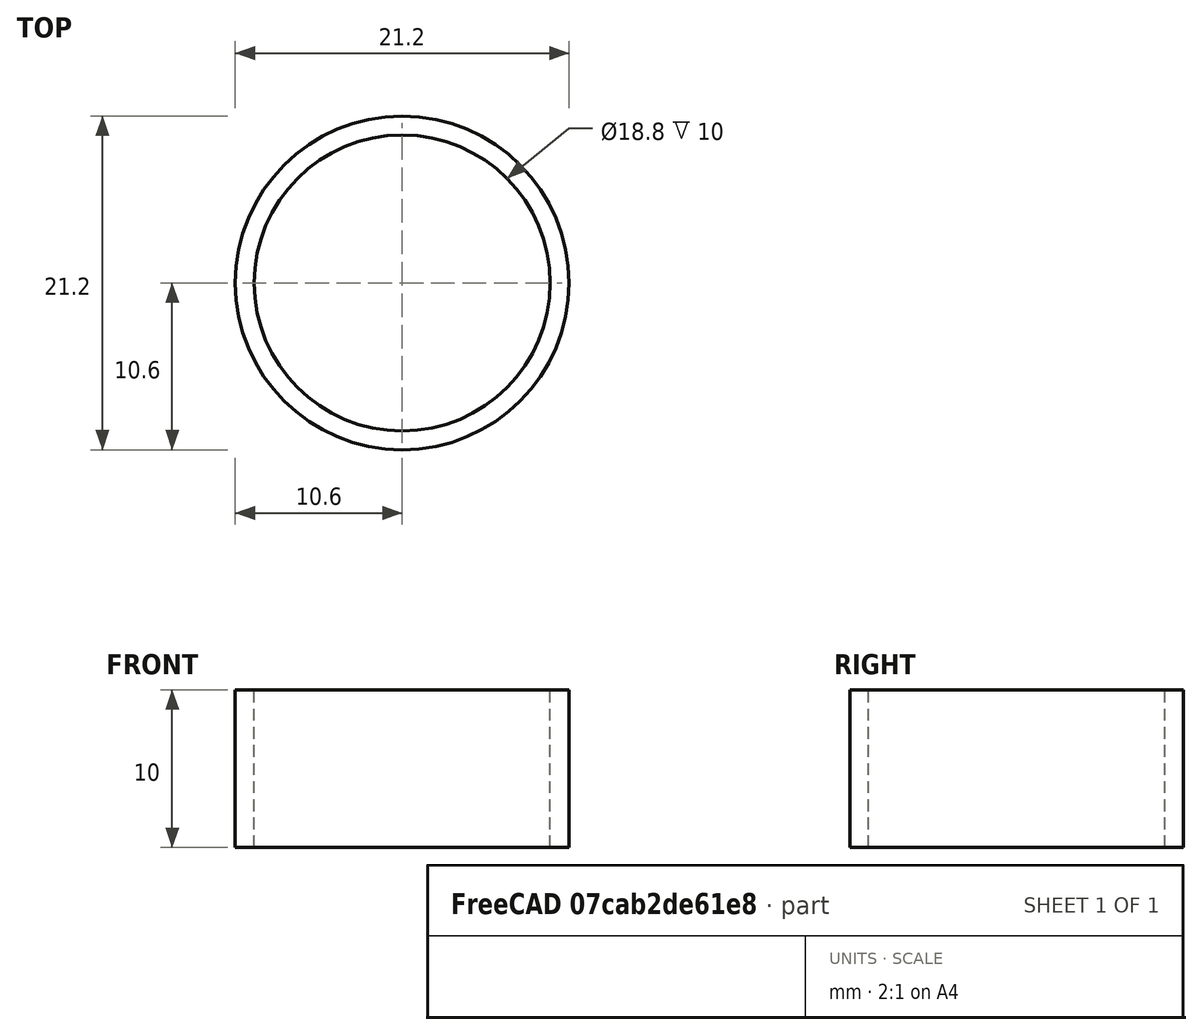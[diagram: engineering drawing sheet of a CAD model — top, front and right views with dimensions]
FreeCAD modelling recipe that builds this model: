
FCSTD DOCUMENT  (FreeCAD 0.20R29177 +426 (Git))
Label: Mag_Spacer_Outer
License: All rights reserved
LicenseURL: http://en.wikipedia.org/wiki/All_rights_reserved
objects: Sketcher::SketchObject×1, PartDesign::Revolution×1, PartDesign::Body×1
note: 4 computed .brp shape members not serialized (recipe doc carries the construction recipe); baked Part::Feature solids carry a one-line shape summary decoded from their .brp

FEATURE [Sketcher::SketchObject] Sketch
  FullyConstrained = true
  MapMode = 5
  Placement = pos=(0,0,0) rot=(1,0,0;1.5708rad)
  Support = -> [XZ_Plane]
  sketch-geometry (4):
    g0: LineSegment StartX=-9.4 StartY=0 StartZ=0 EndX=-9.4 EndY=10 EndZ=0
    g1: LineSegment StartX=-10.6 StartY=10 StartZ=0 EndX=-10.6 EndY=0 EndZ=0
    g2: LineSegment StartX=-9.4 StartY=0 StartZ=0 EndX=-10.6 EndY=0 EndZ=0
    g3: LineSegment StartX=-9.4 StartY=10 StartZ=0 EndX=-10.6 EndY=10 EndZ=0
  constraints (12):
    c: Vertical(g0)
    c: Vertical(g1)
    c: Coincident(g2,g0)
    c: Coincident(g2,g1)
    c: Coincident(g3,g0)
    c: Coincident(g3,g1)
    c: Horizontal(g3)
    c: Horizontal(g2)
    c: DistanceX(g2,g2) = 1.2
    c: DistanceY(g0,g0) = 10
    c: Horizontal(g-1,g0)
    c: DistanceX(g1,g-1) = 10.6
FEATURE [PartDesign::Revolution] Revolution
  Angle = 360
  Axis = (0,-2e-16,1)
  Base = (0,0,0)
  Placement = pos=(0,0,0) rot=(1,0,0;1.5708rad)
  Profile = -> Sketch
  ReferenceAxis = -> Sketch [V_Axis]
FEATURE [PartDesign::Body] Body
  Group = -> [Sketch,Revolution]
  Origin = -> Origin
  Tip = -> Revolution
